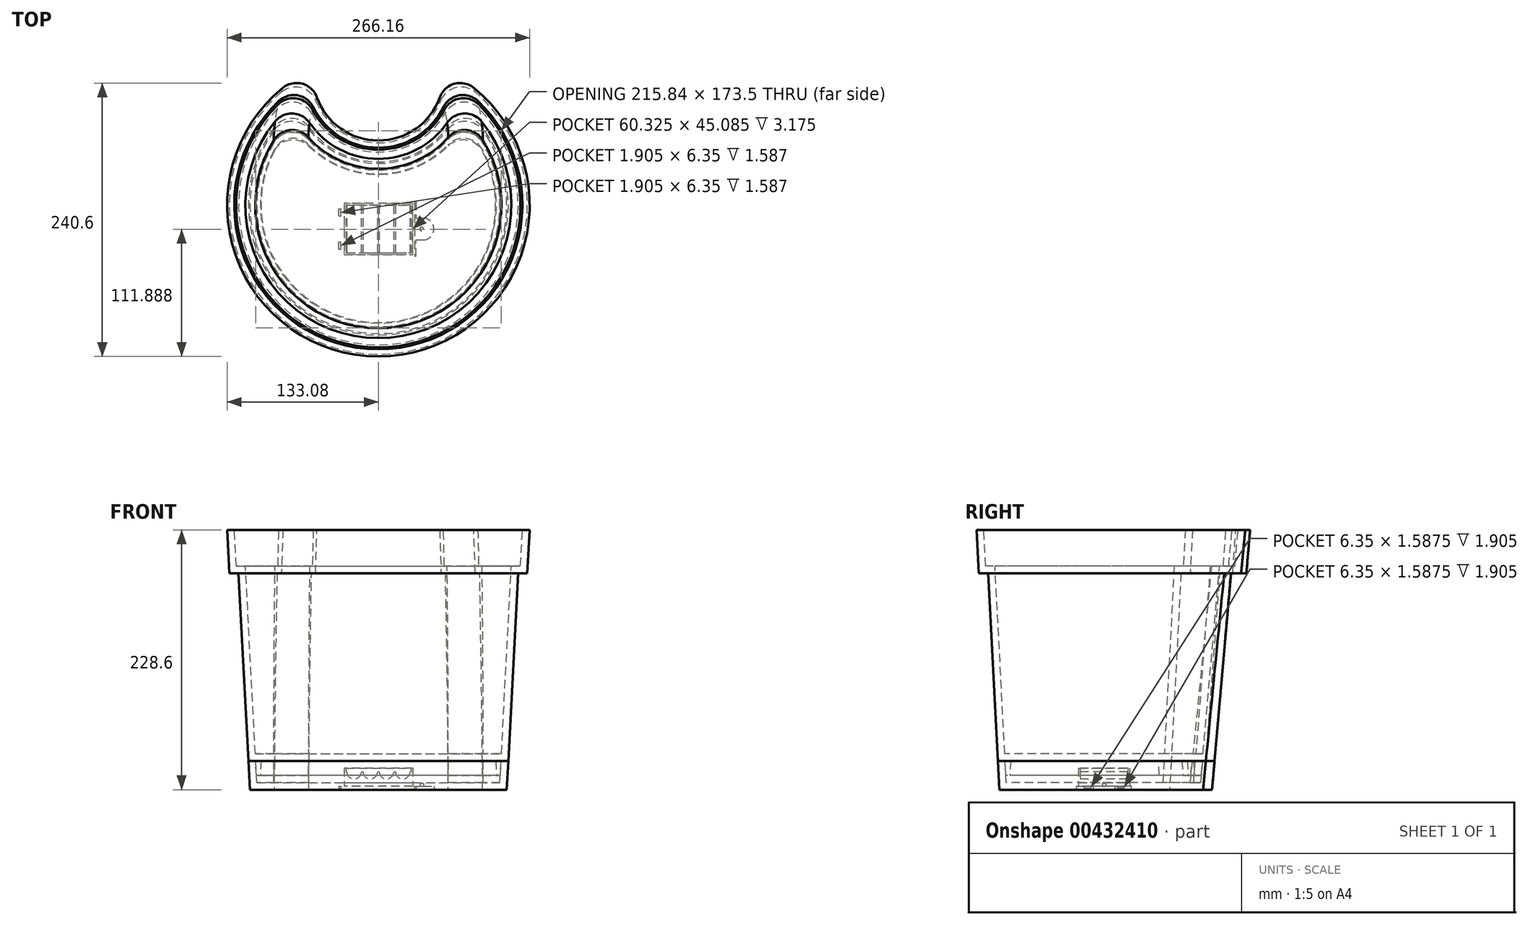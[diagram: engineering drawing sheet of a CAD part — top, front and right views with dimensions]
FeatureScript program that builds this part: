
annotation { "Feature Type Name" : "Feature", "Feature Type Description" : "" }
export const myFeature = defineFeature(function(context is Context, id is Id, definition is map)
    precondition{}
    {
        {
            var Q0;
            Q0=qCreatedBy(makeId("Top.planeOp"),FACE);
            var sketch = newSketch(context, id + "F0", { "sketchPlane" : qUnion([Q0])});
            skArc(sketch, "E0", {"start": v(-71.84, 88.9) * mm, "mid": v(0, -114.3) * mm, "end": v(71.84, 88.9) * mm});
            skArc(sketch, "E1", {"start": v(-71.84, 88.9) * mm, "mid": v(0, 38.1) * mm, "end": v(71.84, 88.9) * mm});
            skSolve(sketch);
        }
        {
            var Q0;
            Q0 = qSketchRegion(id + "F0", true);
            extrude(context, id + "F1", {"entities" : qUnion([Q0]), "depth" : 165.1 * mm, "hasDraft" : true, "draftAngle" : 3 * degree});
        }
        {
            var Q0;
            Q0=makeQuery(id+"F1.opExtrude","CAP_FACE",FACE,{"disambiguationData":[OSD([sQuery(id+"F0.wireOp",EDGE,"E0"),sQuery(id+"F0.wireOp",EDGE,"E1")])],"isStart":false});
            var sketch = newSketch(context, id + "F2", { "sketchPlane" : qUnion([Q0])});
            skArc(sketch, "E2.0", {"start": v(59.36, 116.87) * mm, "mid": v(0, 54.88) * mm, "end": v(-59.36, 116.87) * mm});
            skArc(sketch, "E2.1", {"start": v(-59.36, 116.87) * mm, "mid": v(0, -131.08) * mm, "end": v(59.36, 116.87) * mm});
            skSolve(sketch);
        }
        {
            var Q0;
            Q0 = qSketchRegion(id + "F2", true);
            extrude(context, id + "F3", {"entities" : qUnion([Q0]), "operationType" : NewBodyOperationType.ADD, "depth" : 38.1 * mm, "hasDraft" : true, "draftAngle" : 3 * degree});
        }
        {
            var Q0;
            Q0=makeQuery(id+"F3.opExtrude","CAP_FACE",FACE,{"disambiguationData":[OSD([sQuery(id+"F2.wireOp",EDGE,"E2.0"),sQuery(id+"F2.wireOp",EDGE,"E2.1")])],"isStart":false});
            shell(context, id + "F4", {"entities" : qUnion([Q0]), "thickness" : 6.35 * mm});
        }
        {
            var Q0;
            Q0=makeQuery(id+"F1.opExtrude","CAP_FACE",FACE,{"disambiguationData":[OSD([sQuery(id+"F0.wireOp",EDGE,"E0"),sQuery(id+"F0.wireOp",EDGE,"E1")])],"isStart":true});
            var sketch = newSketch(context, id + "F5", { "sketchPlane" : qUnion([Q0])});
            skArc(sketch, "E3.0", {"start": v(-74.3, -78.32) * mm, "mid": v(0, -31.75) * mm, "end": v(74.3, -78.32) * mm});
            skArc(sketch, "E3.1", {"start": v(74.3, -78.32) * mm, "mid": v(0, 107.95) * mm, "end": v(-74.3, -78.32) * mm});
            skArc(sketch, "E4.0", {"start": v(75.46, -70.38) * mm, "mid": v(0, 103.19) * mm, "end": v(-75.46, -70.38) * mm});
            skArc(sketch, "E4.1", {"start": v(-75.46, -70.38) * mm, "mid": v(0, -26.99) * mm, "end": v(75.46, -70.38) * mm});
            skSolve(sketch);
        }
        {
            var Q0;
            Q0 = qSketchRegion(id + "F5", true);
            extrude(context, id + "F6", {"entities" : qUnion([Q0]), "operationType" : NewBodyOperationType.ADD, "depth" : 12.7 * mm, "hasDraft" : true, "draftAngle" : 3 * degree, "draftPullDirection" : true});
        }
        {
            var Q0;
            Q0=qCreatedBy(makeId("Top.planeOp"),FACE);
            var sketch = newSketch(context, id + "F7", { "sketchPlane" : qUnion([Q0])});
            skArc(sketch, "E5.0", {"start": v(-71.84, 88.9) * mm, "mid": v(0, -114.3) * mm, "end": v(71.84, 88.9) * mm});
            skArc(sketch, "E5.1", {"start": v(-71.84, 88.9) * mm, "mid": v(0, 38.1) * mm, "end": v(71.84, 88.9) * mm});
            skSolve(sketch);
        }
        {
            var Q0;
            Q0 = qSketchRegion(id + "F7", true);
            extrude(context, id + "F8", {"entities" : qUnion([Q0]), "oppositeDirection" : true, "depth" : 25.4 * mm, "hasDraft" : true, "draftAngle" : 3 * degree, "draftPullDirection" : true});
        }
        {
            var Q0;
            Q0=makeQuery(id+"F8.opExtrude","CAP_FACE",FACE,{"disambiguationData":[OSD([sQuery(id+"F7.wireOp",EDGE,"E5.0"),sQuery(id+"F7.wireOp",EDGE,"E5.1")])],"isStart":true});
            shell(context, id + "F9", {"entities" : qUnion([Q0]), "thickness" : 6.35 * mm});
        }
        {
            var Q0;
            {var subQ0=sQuery(id+"F2.wireOp",EDGE,"E2.1");var subQ1=sQuery(id+"F2.wireOp",EDGE,"E2.0");Q0=makeQuery(id+"F3.opExtrude","SWEPT_EDGE",EDGE,{"disambiguationData":[OSD([subQ1,subQ0]),TDD([makeQuery(id+"F2.imprint","INTERSECT",VERTEX,{"disambiguationData":[OD(0.0)],"derivedFrom":[subQ1,subQ0]})])]});}
            var Q1;
            {var subQ0=sQuery(id+"F2.wireOp",EDGE,"E2.1");var subQ1=sQuery(id+"F2.wireOp",EDGE,"E2.0");Q1=makeQuery(id+"F4.opShell","OFFSET_EDGE",EDGE,{"disambiguationData":[OSD([subQ1,subQ0]),TDD([makeQuery(id+"F3.opExtrude","SWEPT_EDGE",EDGE,{"disambiguationData":[OSD([subQ1,subQ0]),TDD([makeQuery(id+"F2.imprint","INTERSECT",VERTEX,{"disambiguationData":[OD(0.0)],"derivedFrom":[subQ1,subQ0]})])]})])]});}
            var Q2;
            {var subQ0=sQuery(id+"F0.wireOp",EDGE,"E1");var subQ1=sQuery(id+"F0.wireOp",EDGE,"E0");Q2=makeQuery(id+"F4.opShell","OFFSET_EDGE",EDGE,{"disambiguationData":[OSD([subQ1,subQ0]),TDD([makeQuery(id+"F1.opExtrude","SWEPT_EDGE",EDGE,{"disambiguationData":[OSD([subQ1,subQ0]),TDD([makeQuery(id+"F0.imprint","INTERSECT",VERTEX,{"disambiguationData":[OD(1.0)],"derivedFrom":[subQ1,subQ0]})])]})])]});}
            var Q3;
            {var subQ0=sQuery(id+"F0.wireOp",EDGE,"E1");var subQ1=sQuery(id+"F0.wireOp",EDGE,"E0");Q3=makeQuery(id+"F4.opShell","OFFSET_EDGE",EDGE,{"disambiguationData":[OSD([subQ1,subQ0]),TDD([makeQuery(id+"F1.opExtrude","SWEPT_EDGE",EDGE,{"disambiguationData":[OSD([subQ1,subQ0]),TDD([makeQuery(id+"F0.imprint","INTERSECT",VERTEX,{"disambiguationData":[OD(0.0)],"derivedFrom":[subQ1,subQ0]})])]})])]});}
            var Q4;
            {var subQ0=sQuery(id+"F2.wireOp",EDGE,"E2.1");var subQ1=sQuery(id+"F2.wireOp",EDGE,"E2.0");Q4=makeQuery(id+"F4.opShell","OFFSET_EDGE",EDGE,{"disambiguationData":[OSD([subQ1,subQ0]),TDD([makeQuery(id+"F3.opExtrude","SWEPT_EDGE",EDGE,{"disambiguationData":[OSD([subQ1,subQ0]),TDD([makeQuery(id+"F2.imprint","INTERSECT",VERTEX,{"disambiguationData":[OD(1.0)],"derivedFrom":[subQ1,subQ0]})])]})])]});}
            var Q5;
            {var subQ0=sQuery(id+"F2.wireOp",EDGE,"E2.1");var subQ1=sQuery(id+"F2.wireOp",EDGE,"E2.0");Q5=makeQuery(id+"F3.opExtrude","SWEPT_EDGE",EDGE,{"disambiguationData":[OSD([subQ1,subQ0]),TDD([makeQuery(id+"F2.imprint","INTERSECT",VERTEX,{"disambiguationData":[OD(1.0)],"derivedFrom":[subQ1,subQ0]})])]});}
            var Q6;
            {var subQ0=sQuery(id+"F0.wireOp",EDGE,"E1");var subQ1=sQuery(id+"F0.wireOp",EDGE,"E0");Q6=makeQuery(id+"F1.opExtrude","SWEPT_EDGE",EDGE,{"disambiguationData":[OSD([subQ1,subQ0]),TDD([makeQuery(id+"F0.imprint","INTERSECT",VERTEX,{"disambiguationData":[OD(0.0)],"derivedFrom":[subQ1,subQ0]})])]});}
            var Q7;
            {var subQ0=sQuery(id+"F5.wireOp",EDGE,"E3.1");var subQ1=sQuery(id+"F5.wireOp",EDGE,"E3.0");Q7=makeQuery(id+"F6.opExtrude","SWEPT_EDGE",EDGE,{"disambiguationData":[OSD([subQ1,subQ0]),TDD([makeQuery(id+"F5.imprint","INTERSECT",VERTEX,{"disambiguationData":[OD(1.0)],"derivedFrom":[subQ1,subQ0]})])]});}
            var Q8;
            {var subQ0=sQuery(id+"F5.wireOp",EDGE,"E4.1");var subQ1=sQuery(id+"F5.wireOp",EDGE,"E4.0");Q8=makeQuery(id+"F6.opExtrude","SWEPT_EDGE",EDGE,{"disambiguationData":[OSD([subQ1,subQ0]),TDD([makeQuery(id+"F5.imprint","INTERSECT",VERTEX,{"disambiguationData":[OD(0.0)],"derivedFrom":[subQ1,subQ0]})])]});}
            var Q9;
            {var subQ0=sQuery(id+"F5.wireOp",EDGE,"E3.1");var subQ1=sQuery(id+"F5.wireOp",EDGE,"E3.0");Q9=makeQuery(id+"F6.opExtrude","SWEPT_EDGE",EDGE,{"disambiguationData":[OSD([subQ1,subQ0]),TDD([makeQuery(id+"F5.imprint","INTERSECT",VERTEX,{"disambiguationData":[OD(0.0)],"derivedFrom":[subQ1,subQ0]})])]});}
            var Q10;
            {var subQ0=sQuery(id+"F5.wireOp",EDGE,"E4.1");var subQ1=sQuery(id+"F5.wireOp",EDGE,"E4.0");Q10=makeQuery(id+"F6.opExtrude","SWEPT_EDGE",EDGE,{"disambiguationData":[OSD([subQ1,subQ0]),TDD([makeQuery(id+"F5.imprint","INTERSECT",VERTEX,{"disambiguationData":[OD(1.0)],"derivedFrom":[subQ1,subQ0]})])]});}
            var Q11;
            {var subQ0=sQuery(id+"F0.wireOp",EDGE,"E1");var subQ1=sQuery(id+"F0.wireOp",EDGE,"E0");Q11=makeQuery(id+"F1.opExtrude","SWEPT_EDGE",EDGE,{"disambiguationData":[OSD([subQ1,subQ0]),TDD([makeQuery(id+"F0.imprint","INTERSECT",VERTEX,{"disambiguationData":[OD(1.0)],"derivedFrom":[subQ1,subQ0]})])]});}
            var Q12;
            {var subQ0=sQuery(id+"F7.wireOp",EDGE,"E5.1");var subQ1=sQuery(id+"F7.wireOp",EDGE,"E5.0");Q12=makeQuery(id+"F8.opExtrude","SWEPT_EDGE",EDGE,{"disambiguationData":[OSD([subQ1,subQ0]),TDD([makeQuery(id+"F7.imprint","INTERSECT",VERTEX,{"disambiguationData":[OD(1.0)],"derivedFrom":[subQ1,subQ0]})])]});}
            var Q13;
            {var subQ0=sQuery(id+"F7.wireOp",EDGE,"E5.1");var subQ1=sQuery(id+"F7.wireOp",EDGE,"E5.0");Q13=makeQuery(id+"F9.opShell","OFFSET_EDGE",EDGE,{"disambiguationData":[OSD([subQ1,subQ0]),TDD([makeQuery(id+"F8.opExtrude","SWEPT_EDGE",EDGE,{"disambiguationData":[OSD([subQ1,subQ0]),TDD([makeQuery(id+"F7.imprint","INTERSECT",VERTEX,{"disambiguationData":[OD(1.0)],"derivedFrom":[subQ1,subQ0]})])]})])]});}
            var Q14;
            {var subQ0=sQuery(id+"F7.wireOp",EDGE,"E5.1");var subQ1=sQuery(id+"F7.wireOp",EDGE,"E5.0");Q14=makeQuery(id+"F8.opExtrude","SWEPT_EDGE",EDGE,{"disambiguationData":[OSD([subQ1,subQ0]),TDD([makeQuery(id+"F7.imprint","INTERSECT",VERTEX,{"disambiguationData":[OD(0.0)],"derivedFrom":[subQ1,subQ0]})])]});}
            var Q15;
            {var subQ0=sQuery(id+"F7.wireOp",EDGE,"E5.1");var subQ1=sQuery(id+"F7.wireOp",EDGE,"E5.0");Q15=makeQuery(id+"F9.opShell","OFFSET_EDGE",EDGE,{"disambiguationData":[OSD([subQ1,subQ0]),TDD([makeQuery(id+"F8.opExtrude","SWEPT_EDGE",EDGE,{"disambiguationData":[OSD([subQ1,subQ0]),TDD([makeQuery(id+"F7.imprint","INTERSECT",VERTEX,{"disambiguationData":[OD(0.0)],"derivedFrom":[subQ1,subQ0]})])]})])]});}
            fillet(context, id + "F10", {"entities" : qUnion([Q0, Q1, Q2, Q3, Q4, Q5, Q6, Q7, Q8, Q9, Q10, Q11, Q12, Q13, Q14, Q15]), "radius" : 19.05 * mm, "tangentPropagation" : true, "allowEdgeOverflow" : false});
        }
        {
            var Q0;
            Q0=makeQuery(id+"F9.opShell","OFFSET_FACE",FACE,{"disambiguationData":[OSD([sQuery(id+"F7.wireOp",EDGE,"E5.0"),sQuery(id+"F7.wireOp",EDGE,"E5.1")])]});
            var sketch = newSketch(context, id + "F11", { "sketchPlane" : qUnion([Q0])});
            skLineSegment(sketch, "E6.bottom", {"start": v(-28.58, 0) * mm, "end": v(28.57, 0) * mm});
            skLineSegment(sketch, "E6.top", {"start": v(-28.58, -41.91) * mm, "end": v(28.57, -41.91) * mm});
            skLineSegment(sketch, "E6.left", {"start": v(-28.58, 0) * mm, "end": v(-28.58, -41.91) * mm});
            skLineSegment(sketch, "E6.right", {"start": v(28.57, 0) * mm, "end": v(28.57, -41.91) * mm});
            skSolve(sketch);
        }
        {
            var Q0;
            Q0 = qSketchRegion(id + "F11", true);
            extrude(context, id + "F12", {"entities" : qUnion([Q0]), "depth" : 15.88 * mm});
        }
        {
            var Q0;
            Q0=makeQuery(id+"F12.opExtrude","SWEPT_FACE",FACE,{"disambiguationData":[OSD([sQuery(id+"F11.wireOp",EDGE,"E6.top")])]});
            var sketch = newSketch(context, id + "F13", { "sketchPlane" : qUnion([Q0])});
            skLineSegment(sketch, "E7", {"start": v(-28.58, -15.88) * mm, "end": v(28.57, -15.88) * mm, "construction": true});
            skArc(sketch, "E8", {"start": v(-27.78, -9.52) * mm, "mid": v(-21.43, -15.88) * mm, "end": v(-15.08, -9.52) * mm});
            skArc(sketch, "E9", {"start": v(-13.5, -9.52) * mm, "mid": v(-7.14, -15.88) * mm, "end": v(-0.8, -9.52) * mm});
            skArc(sketch, "E10", {"start": v(0.8, -9.52) * mm, "mid": v(7.14, -15.88) * mm, "end": v(13.5, -9.52) * mm});
            skArc(sketch, "E11", {"start": v(15.08, -9.52) * mm, "mid": v(21.43, -15.88) * mm, "end": v(27.78, -9.52) * mm});
            skLineSegment(sketch, "E12", {"start": v(-28.58, -9.52) * mm, "end": v(-27.78, -9.52) * mm});
            skLineSegment(sketch, "E13.trimOffspring", {"start": v(27.78, -9.52) * mm, "end": v(28.57, -9.52) * mm});
            skLineSegment(sketch, "E14.trimOffspring", {"start": v(13.5, -9.52) * mm, "end": v(15.08, -9.52) * mm});
            skLineSegment(sketch, "E15.trimOffspring", {"start": v(-0.8, -9.52) * mm, "end": v(0.8, -9.52) * mm});
            skLineSegment(sketch, "E16.trimOffspring", {"start": v(-15.08, -9.52) * mm, "end": v(-13.5, -9.52) * mm});
            skLineSegment(sketch, "E17", {"start": v(-28.58, -9.52) * mm, "end": v(-28.58, -3.18) * mm});
            skLineSegment(sketch, "E18", {"start": v(-28.58, -3.18) * mm, "end": v(28.58, -3.17) * mm});
            skLineSegment(sketch, "E19", {"start": v(28.58, -3.18) * mm, "end": v(28.58, -9.52) * mm});
            skSolve(sketch);
        }
        {
            var Q0;
            Q0 = qSketchRegion(id + "F13", true);
            var Q1;
            Q1=makeQuery(id+"F13.imprint","IMPRINT",FACE,{"disambiguationData":[TD([[makeQuery(id+"F13.imprint","IMPRINT",EDGE,{"derivedFrom":sQuery(id+"F13.wireOp",EDGE,"E9")}),1.0]])]});
            var Q2;
            Q2=makeQuery(id+"F13.imprint","IMPRINT",FACE,{"disambiguationData":[TD([[makeQuery(id+"F13.imprint","IMPRINT",EDGE,{"derivedFrom":sQuery(id+"F13.wireOp",EDGE,"E8")}),1.0]])]});
            var Q3;
            Q3=makeQuery(id+"F13.imprint","IMPRINT",FACE,{"disambiguationData":[TD([[makeQuery(id+"F13.imprint","IMPRINT",EDGE,{"derivedFrom":sQuery(id+"F13.wireOp",EDGE,"E10")}),1.0]])]});
            var Q4;
            {var subQ0=sQuery(id+"F13.wireOp",EDGE,"E11");var subQ1=sQuery(id+"F11.wireOp",EDGE,"E6.top");var subQ2=makeQuery(id+"F13.imprint","INTERSECT",VERTEX,{"derivedFrom":[makeQuery(id+"F12.opExtrude","CAP_EDGE",EDGE,{"disambiguationData":[OSD([subQ1])],"isStart":false}),subQ0]});Q4=makeQuery(id+"F13.imprint","IMPRINT",FACE,{"disambiguationData":[TD([[makeQuery(id+"F13.imprint","IMPRINT",EDGE,{"disambiguationData":[TD([[subQ2,1.0]])],"derivedFrom":subQ0}),1.0]])]});}
            extrude(context, id + "F14", {"entities" : qUnion([Q0, Q1, Q2, Q3, Q4]), "operationType" : NewBodyOperationType.REMOVE, "oppositeDirection" : true, "depth" : 49.02 * mm});
        }
        {
            var Q0;
            Q0=makeQuery(id+"F12.opExtrude","CAP_FACE",FACE,{"disambiguationData":[OSD([sQuery(id+"F11.wireOp",EDGE,"E6.bottom"),sQuery(id+"F11.wireOp",EDGE,"E6.top"),sQuery(id+"F11.wireOp",EDGE,"E6.left"),sQuery(id+"F11.wireOp",EDGE,"E6.right")])],"isStart":true});
            var sketch = newSketch(context, id + "F15", { "sketchPlane" : qUnion([Q0])});
            skLineSegment(sketch, "E20.0", {"start": v(-28.58, 41.91) * mm, "end": v(28.57, 41.91) * mm});
            skLineSegment(sketch, "E20.1", {"start": v(-28.58, 0) * mm, "end": v(-28.58, 41.91) * mm});
            skLineSegment(sketch, "E20.2", {"start": v(28.57, 0) * mm, "end": v(28.57, 41.91) * mm});
            skLineSegment(sketch, "E20.3", {"start": v(-28.58, 0) * mm, "end": v(28.57, 0) * mm});
            skLineSegment(sketch, "E21.0", {"start": v(-30.16, 43.5) * mm, "end": v(-30.16, -1.59) * mm});
            skLineSegment(sketch, "E21.1", {"start": v(30.16, 43.5) * mm, "end": v(-30.16, 43.5) * mm});
            skLineSegment(sketch, "E21.2", {"start": v(30.16, -1.59) * mm, "end": v(30.16, 43.5) * mm});
            skLineSegment(sketch, "E21.3", {"start": v(-30.16, -1.59) * mm, "end": v(30.16, -1.59) * mm});
            skSolve(sketch);
        }
        {
            var Q0;
            Q0 = qSketchRegion(id + "F15", true);
            extrude(context, id + "F16", {"entities" : qUnion([Q0]), "operationType" : NewBodyOperationType.ADD, "oppositeDirection" : true, "depth" : 12.7 * mm});
        }
        {
            var Q0;
            Q0=makeQuery(id+"F8.opExtrude","CAP_FACE",FACE,{"disambiguationData":[OSD([sQuery(id+"F7.wireOp",EDGE,"E5.0"),sQuery(id+"F7.wireOp",EDGE,"E5.1")])],"isStart":false});
            var sketch = newSketch(context, id + "F17", { "sketchPlane" : qUnion([Q0])});
            skLineSegment(sketch, "E22.0", {"start": v(30.16, 43.5) * mm, "end": v(-30.16, 43.5) * mm});
            skLineSegment(sketch, "E22.1", {"start": v(-30.16, 43.5) * mm, "end": v(-30.16, -1.59) * mm});
            skLineSegment(sketch, "E22.2", {"start": v(-30.16, -1.59) * mm, "end": v(30.16, -1.59) * mm});
            skLineSegment(sketch, "E22.3", {"start": v(30.16, -1.59) * mm, "end": v(30.16, 43.5) * mm});
            skSolve(sketch);
        }
        {
            var Q0;
            Q0 = qSketchRegion(id + "F17", true);
            extrude(context, id + "F18", {"entities" : qUnion([Q0]), "operationType" : NewBodyOperationType.REMOVE, "oppositeDirection" : true, "depth" : 6.35 * mm});
        }
        {
            var Q0;
            Q0=makeQuery(id+"F8.opExtrude","CAP_FACE",FACE,{"disambiguationData":[OSD([sQuery(id+"F7.wireOp",EDGE,"E5.0"),sQuery(id+"F7.wireOp",EDGE,"E5.1")])],"isStart":false});
            var sketch = newSketch(context, id + "F19", { "sketchPlane" : qUnion([Q0])});
            skLineSegment(sketch, "E23.0", {"start": v(31.75, 45.09) * mm, "end": v(-31.75, 45.09) * mm});
            skLineSegment(sketch, "E23.1", {"start": v(31.75, -3.17) * mm, "end": v(31.75, 45.09) * mm});
            skLineSegment(sketch, "E23.2", {"start": v(-31.75, -3.17) * mm, "end": v(31.75, -3.17) * mm});
            skLineSegment(sketch, "E23.3", {"start": v(-31.75, 45.09) * mm, "end": v(-31.75, -3.17) * mm});
            skSolve(sketch);
        }
        {
            var Q0;
            Q0 = qSketchRegion(id + "F19", true);
            extrude(context, id + "F20", {"entities" : qUnion([Q0]), "operationType" : NewBodyOperationType.REMOVE, "oppositeDirection" : true, "depth" : 3.17 * mm});
        }
        {
            var Q0;
            Q0=makeQuery(id+"F8.opExtrude","CAP_FACE",FACE,{"disambiguationData":[OSD([sQuery(id+"F7.wireOp",EDGE,"E5.0"),sQuery(id+"F7.wireOp",EDGE,"E5.1")])],"isStart":false});
            var sketch = newSketch(context, id + "F21", { "sketchPlane" : qUnion([Q0])});
            skCircle(sketch, "E24", {"center": v(38.1, 20.96) * mm, "radius": 9.53 * mm});
            skPoint(sketch, "E24.centerSnap0", {"position": v(31.75, 20.96) * mm});
            skLineSegment(sketch, "E25.bottom", {"start": v(31.75, 30.48) * mm, "end": v(38.1, 30.48) * mm});
            skLineSegment(sketch, "E25.top", {"start": v(31.75, 11.43) * mm, "end": v(38.1, 11.43) * mm});
            skLineSegment(sketch, "E25.left", {"start": v(31.75, 30.48) * mm, "end": v(31.75, 11.43) * mm});
            skLineSegment(sketch, "E25.right", {"start": v(38.1, 30.48) * mm, "end": v(38.1, 11.43) * mm});
            skSolve(sketch);
        }
        {
            var Q0;
            Q0 = qSketchRegion(id + "F21", true);
            extrude(context, id + "F22", {"entities" : qUnion([Q0]), "operationType" : NewBodyOperationType.REMOVE, "oppositeDirection" : true, "depth" : 3.17 * mm});
        }
        {
            var Q0;
            Q0=makeQuery(id+"F20.boolean.opBoolean","COPY",FACE,{"derivedFrom":makeQuery(id+"F20.opExtrude","SWEPT_FACE",FACE,{"disambiguationData":[OSD([sQuery(id+"F19.wireOp",EDGE,"E23.3")])]})});
            var sketch = newSketch(context, id + "F23", { "sketchPlane" : qUnion([Q0])});
            skLineSegment(sketch, "E26.bottom", {"start": v(-3.18, -22.23) * mm, "end": v(-9.53, -22.23) * mm});
            skLineSegment(sketch, "E26.top", {"start": v(-3.18, -23.81) * mm, "end": v(-9.53, -23.81) * mm});
            skLineSegment(sketch, "E26.left", {"start": v(-3.18, -22.23) * mm, "end": v(-3.18, -23.81) * mm});
            skLineSegment(sketch, "E26.right", {"start": v(-9.53, -22.23) * mm, "end": v(-9.53, -23.81) * mm});
            skLineSegment(sketch, "E27", {"start": v(-20.96, -22.23) * mm, "end": v(-20.96, -25.4) * mm, "construction": true});
            skLineSegment(sketch, "E28.MirrorCS", {"start": v(-38.74, -23.81) * mm, "end": v(-32.39, -23.81) * mm});
            skLineSegment(sketch, "E29.MirrorCS", {"start": v(-32.38, -22.23) * mm, "end": v(-32.38, -23.81) * mm});
            skLineSegment(sketch, "E30.MirrorCS", {"start": v(-38.74, -22.23) * mm, "end": v(-32.39, -22.23) * mm});
            skLineSegment(sketch, "E31.MirrorCS", {"start": v(-38.73, -22.23) * mm, "end": v(-38.73, -23.81) * mm});
            skSolve(sketch);
        }
        {
            var Q0;
            Q0 = qSketchRegion(id + "F23", true);
            extrude(context, id + "F24", {"entities" : qUnion([Q0]), "operationType" : NewBodyOperationType.REMOVE, "oppositeDirection" : true, "depth" : 3.17 * mm});
        }
        {
            var Q0;
            Q0=makeQuery(id+"F24.boolean.opBoolean","MERGE",FACE,{"derivedFrom":[makeQuery(id+"F22.boolean.opBoolean","MERGE",FACE,{"derivedFrom":[makeQuery(id+"F20.boolean.opBoolean","COPY",FACE,{"derivedFrom":makeQuery(id+"F20.opExtrude","CAP_FACE",FACE,{"disambiguationData":[OSD([sQuery(id+"F19.wireOp",EDGE,"E23.0"),sQuery(id+"F19.wireOp",EDGE,"E23.1"),sQuery(id+"F19.wireOp",EDGE,"E23.2"),sQuery(id+"F19.wireOp",EDGE,"E23.3")])],"isStart":false})}),makeQuery(id+"F22.opExtrude","CAP_FACE",FACE,{"disambiguationData":[OSD([sQuery(id+"F21.wireOp",EDGE,"E24"),sQuery(id+"F21.wireOp",EDGE,"E25.bottom"),sQuery(id+"F21.wireOp",EDGE,"E25.top"),sQuery(id+"F21.wireOp",EDGE,"E25.left")])],"isStart":false})]}),makeQuery(id+"F24.opExtrude","SWEPT_FACE",FACE,{"disambiguationData":[OSD([sQuery(id+"F23.wireOp",EDGE,"E26.bottom")])]}),makeQuery(id+"F24.opExtrude","SWEPT_FACE",FACE,{"disambiguationData":[OSD([sQuery(id+"F23.wireOp",EDGE,"E30.MirrorCS")])]})]});
            var sketch = newSketch(context, id + "F25", { "sketchPlane" : qUnion([Q0])});
            skCircle(sketch, "E32", {"center": v(38.1, 20.96) * mm, "radius": 1.59 * mm});
            skSolve(sketch);
        }
        {
            var Q0;
            Q0 = qSketchRegion(id + "F25", true);
            extrude(context, id + "F26", {"entities" : qUnion([Q0]), "operationType" : NewBodyOperationType.REMOVE, "oppositeDirection" : true, "depth" : 2.54 * mm});
        }
        {
            var Q0;
            Q0=makeQuery(id+"F24.boolean.opBoolean","MERGE",FACE,{"derivedFrom":[makeQuery(id+"F22.boolean.opBoolean","MERGE",FACE,{"derivedFrom":[makeQuery(id+"F20.boolean.opBoolean","COPY",FACE,{"derivedFrom":makeQuery(id+"F20.opExtrude","CAP_FACE",FACE,{"disambiguationData":[OSD([sQuery(id+"F19.wireOp",EDGE,"E23.0"),sQuery(id+"F19.wireOp",EDGE,"E23.1"),sQuery(id+"F19.wireOp",EDGE,"E23.2"),sQuery(id+"F19.wireOp",EDGE,"E23.3")])],"isStart":false})}),makeQuery(id+"F22.opExtrude","CAP_FACE",FACE,{"disambiguationData":[OSD([sQuery(id+"F21.wireOp",EDGE,"E24"),sQuery(id+"F21.wireOp",EDGE,"E25.bottom"),sQuery(id+"F21.wireOp",EDGE,"E25.top"),sQuery(id+"F21.wireOp",EDGE,"E25.left")])],"isStart":false})]}),makeQuery(id+"F24.opExtrude","SWEPT_FACE",FACE,{"disambiguationData":[OSD([sQuery(id+"F23.wireOp",EDGE,"E26.bottom")])]}),makeQuery(id+"F24.opExtrude","SWEPT_FACE",FACE,{"disambiguationData":[OSD([sQuery(id+"F23.wireOp",EDGE,"E30.MirrorCS")])]})]});
            var sketch = newSketch(context, id + "F27", { "sketchPlane" : qUnion([Q0])});
            skLineSegment(sketch, "E33.bottom", {"start": v(-31.75, 45.09) * mm, "end": v(31.75, 45.09) * mm});
            skLineSegment(sketch, "E33.top", {"start": v(-31.75, -3.17) * mm, "end": v(31.75, -3.17) * mm});
            skLineSegment(sketch, "E33.left", {"start": v(-31.75, 45.09) * mm, "end": v(-31.75, -3.17) * mm});
            skLineSegment(sketch, "E33.right", {"start": v(31.75, 45.09) * mm, "end": v(31.75, 30.48) * mm});
            skLineSegment(sketch, "E34.0", {"start": v(31.75, 30.48) * mm, "end": v(38.1, 30.48) * mm});
            skArc(sketch, "E35.0", {"start": v(38.1, 11.43) * mm, "mid": v(47.62, 20.96) * mm, "end": v(38.1, 30.48) * mm});
            skLineSegment(sketch, "E36.0", {"start": v(31.75, 11.43) * mm, "end": v(38.1, 11.43) * mm});
            skCircle(sketch, "E37.0", {"center": v(38.1, 20.96) * mm, "radius": 1.59 * mm});
            skLineSegment(sketch, "E38.trimOffspring", {"start": v(31.75, 11.43) * mm, "end": v(31.75, -3.17) * mm});
            skSolve(sketch);
        }
        {
            var Q0;
            Q0 = qSketchRegion(id + "F27", true);
            var Q1;
            Q1=makeQuery(id+"F8.opExtrude","CAP_FACE",FACE,{"disambiguationData":[OSD([sQuery(id+"F7.wireOp",EDGE,"E5.0"),sQuery(id+"F7.wireOp",EDGE,"E5.1")])],"isStart":false});
            extrude(context, id + "F28", {"entities" : qUnion([Q0]), "endBound" : BoundingType.UP_TO_SURFACE, "endBoundEntityFace" : qUnion([Q1]), "depth" : 25.4 * mm});
        }
        {
            var Q0;
            Q0=makeQuery(id+"F8.opExtrude","CAP_FACE",FACE,{"disambiguationData":[OSD([sQuery(id+"F7.wireOp",EDGE,"E5.0"),sQuery(id+"F7.wireOp",EDGE,"E5.1")])],"isStart":false});
            var sketch = newSketch(context, id + "F29", { "sketchPlane" : qUnion([Q0])});
            skLineSegment(sketch, "E39", {"start": v(33.02, 45.09) * mm, "end": v(33.02, 30.48) * mm});
            skPoint(sketch, "E40.centerSnap0", {"position": v(47.62, 20.96) * mm});
            skLineSegment(sketch, "E41", {"start": v(33.02, 30.48) * mm, "end": v(39.37, 30.48) * mm});
            skLineSegment(sketch, "E42", {"start": v(33.02, 45.09) * mm, "end": v(31.75, 45.09) * mm});
            skLineSegment(sketch, "E43", {"start": v(31.75, 45.09) * mm, "end": v(31.75, -3.17) * mm});
            skLineSegment(sketch, "E44", {"start": v(31.75, -3.17) * mm, "end": v(33.02, -3.17) * mm});
            skLineSegment(sketch, "E45", {"start": v(33.02, -3.17) * mm, "end": v(33.02, 11.43) * mm});
            skLineSegment(sketch, "E46", {"start": v(33.02, 11.43) * mm, "end": v(39.37, 11.43) * mm});
            skArc(sketch, "E47.trimOffspring", {"start": v(39.37, 11.43) * mm, "mid": v(48.9, 20.96) * mm, "end": v(39.37, 30.48) * mm});
            skSolve(sketch);
        }
        {
            var Q0;
            Q0 = qSketchRegion(id + "F29", true);
            extrude(context, id + "F30", {"entities" : qUnion([Q0]), "operationType" : NewBodyOperationType.REMOVE, "oppositeDirection" : true, "depth" : 3.17 * mm});
        }
        {
            var Q0;
            Q0=makeQuery(id+"F28.opExtrude","SWEPT_FACE",FACE,{"disambiguationData":[OSD([sQuery(id+"F27.wireOp",EDGE,"E33.left")])]});
            var sketch = newSketch(context, id + "F31", { "sketchPlane" : qUnion([Q0])});
            skLineSegment(sketch, "E48.0", {"start": v(3.18, -22.23) * mm, "end": v(3.18, -23.81) * mm});
            skLineSegment(sketch, "E48.1", {"start": v(3.18, -23.81) * mm, "end": v(9.53, -23.81) * mm});
            skLineSegment(sketch, "E48.2", {"start": v(9.53, -22.23) * mm, "end": v(9.53, -23.81) * mm});
            skLineSegment(sketch, "E48.3", {"start": v(38.73, -22.23) * mm, "end": v(38.73, -23.81) * mm});
            skLineSegment(sketch, "E48.4", {"start": v(38.74, -23.81) * mm, "end": v(32.39, -23.81) * mm});
            skLineSegment(sketch, "E48.5", {"start": v(32.38, -22.23) * mm, "end": v(32.38, -23.81) * mm});
            skLineSegment(sketch, "E48.6", {"start": v(38.74, -22.23) * mm, "end": v(32.38, -22.23) * mm});
            skLineSegment(sketch, "E48.7", {"start": v(9.53, -22.23) * mm, "end": v(3.18, -22.23) * mm});
            skSolve(sketch);
        }
        {
            var Q0;
            Q0 = qSketchRegion(id + "F31", true);
            extrude(context, id + "F32", {"entities" : qUnion([Q0]), "operationType" : NewBodyOperationType.ADD, "depth" : 1.27 * mm});
        }
    });
